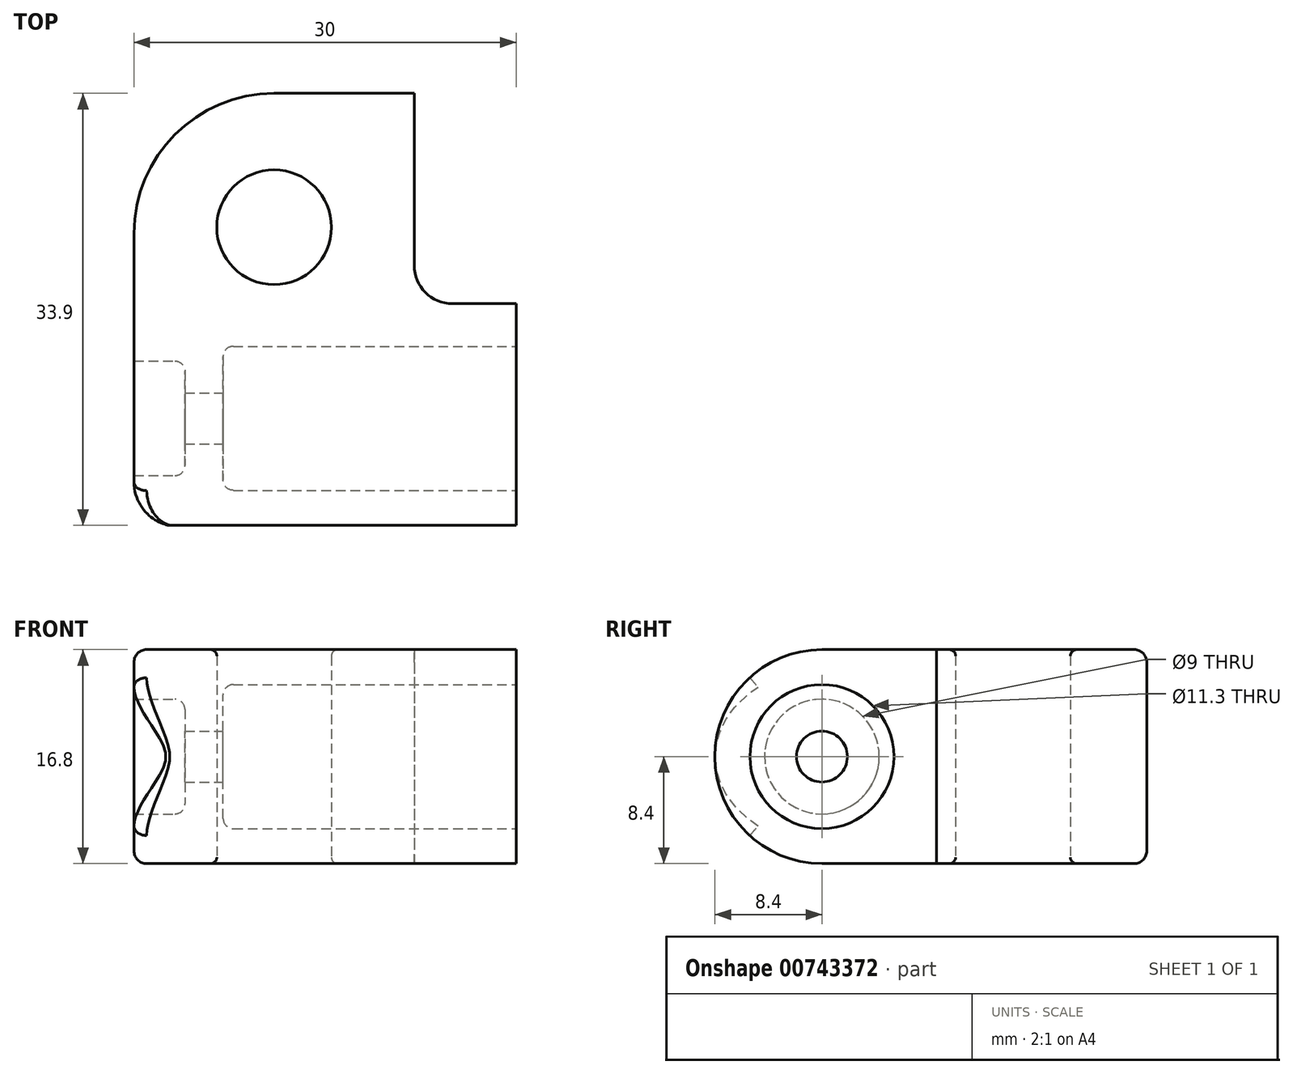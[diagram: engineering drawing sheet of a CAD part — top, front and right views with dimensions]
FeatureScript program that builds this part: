
annotation { "Feature Type Name" : "Feature", "Feature Type Description" : "" }
export const myFeature = defineFeature(function(context is Context, id is Id, definition is map)
    precondition{}
    {
        {
            var Q0;
            Q0=qCreatedBy(makeId("Top.planeOp"),FACE);
            var sketch = newSketch(context, id + "F0", { "sketchPlane" : qUnion([Q0]), "disableImprinting" : false});
            skLineSegment(sketch, "E0.bottom", {"start": v(-11, 10.5) * mm, "end": v(11, 10.5) * mm});
            skLineSegment(sketch, "E0.top", {"start": v(-11, -23.5) * mm, "end": v(19, -23.5) * mm});
            skLineSegment(sketch, "E0.left", {"start": v(-11, 10.5) * mm, "end": v(-11, -23.5) * mm});
            skLineSegment(sketch, "E0.right", {"start": v(19, -6) * mm, "end": v(19, -23.5) * mm});
            skCircle(sketch, "E1", {"center": v(0, 0) * mm, "radius": 4.5 * mm});
            skLineSegment(sketch, "E2.top", {"start": v(11, -6) * mm, "end": v(19, -6) * mm});
            skLineSegment(sketch, "E2.left", {"start": v(11, 10.5) * mm, "end": v(11, -6) * mm});
            skSolve(sketch);
        }
        {
            var Q0;
            Q0=makeQuery(id+"F0.imprint","IMPRINT",FACE,{"disambiguationData":[TD([[makeQuery(id+"F0.imprint","IMPRINT",EDGE,{"derivedFrom":sQuery(id+"F0.wireOp",EDGE,"E0.bottom")}),-1.0]])]});
            extrude(context, id + "F1", {"entities" : qUnion([Q0]), "flatOperationType" : FlatOperationType.REMOVE, "thickness1" : 5 * mm, "thickness2" : 0 * mm, "thickness" : 5 * mm, "offsetDistance" : 25 * mm, "startOffsetBound" : StartOffsetType.BLIND, "startOffsetDistance" : 25 * mm, "depth" : 16.8 * mm, "symmetric" : true, "domain" : OperationDomain.MODEL});
        }
        {
            var Q0;
            Q0=makeQuery(id+"F1.opExtrude","SWEPT_EDGE",EDGE,{"disambiguationData":[OSD([sQuery(id+"F0.wireOp",EDGE,"E2.top"),sQuery(id+"F0.wireOp",EDGE,"E2.left")])]});
            fillet(context, id + "F2", {"entities" : qUnion([Q0]), "radius" : 3 * mm, "tangentPropagation" : true, "allowEdgeOverflow" : false});
        }
        {
            var Q0;
            Q0=makeQuery(id+"F1.opExtrude","SWEPT_EDGE",EDGE,{"disambiguationData":[OSD([sQuery(id+"F0.wireOp",EDGE,"E0.bottom"),sQuery(id+"F0.wireOp",EDGE,"E0.left")])]});
            fillet(context, id + "F3", {"entities" : qUnion([Q0]), "radius" : 11 * mm, "tangentPropagation" : true, "allowEdgeOverflow" : false});
        }
        {
            var Q0;
            Q0=qCreatedBy(makeId("Top.planeOp"),FACE);
            var sketch = newSketch(context, id + "F4", { "sketchPlane" : qUnion([Q0]), "disableImprinting" : false});
            skLineSegment(sketch, "E3.0", {"start": v(-11, -0.5) * mm, "end": v(-11, -23.5) * mm});
            skPoint(sketch, "E4.trimOffspring.end.orphan", {"position": v(19, -23.5) * mm});
            skLineSegment(sketch, "E5", {"start": v(-11, -10.5) * mm, "end": v(-7, -10.5) * mm});
            skLineSegment(sketch, "E6", {"start": v(-7, -10.5) * mm, "end": v(-7, -13) * mm});
            skLineSegment(sketch, "E7", {"start": v(-7, -13) * mm, "end": v(-4, -13) * mm});
            skLineSegment(sketch, "E8", {"start": v(-4, -13) * mm, "end": v(-4, -9.35) * mm});
            skLineSegment(sketch, "E9.0", {"start": v(19, -6) * mm, "end": v(19, -23.5) * mm});
            skLineSegment(sketch, "E10", {"start": v(-4, -9.35) * mm, "end": v(19, -9.35) * mm});
            skLineSegment(sketch, "E11", {"start": v(-11, -10.5) * mm, "end": v(-11, -15) * mm});
            skLineSegment(sketch, "E12", {"start": v(19, -15) * mm, "end": v(19, -9.35) * mm});
            skLineSegment(sketch, "E13", {"start": v(-11, -15) * mm, "end": v(19, -15) * mm});
            skSolve(sketch);
        }
        {
            var Q0;
            Q0=qSketchRegion(id+"F4",true);
            var Q1;
            Q1=sQuery(id+"F4.wireOp",EDGE,"E13");
            revolve(context, id + "F5", {"operationType" : NewBodyOperationType.REMOVE, "entities" : qUnion([Q0]), "axis" : qUnion([Q1]), "revolveType" : RevolveType.FULL, "oppositeDirection" : true});
        }
        {
            var Q0;
            Q0=makeQuery(id+"F1.opExtrude","SWEPT_EDGE",EDGE,{"disambiguationData":[OSD([sQuery(id+"F0.wireOp",EDGE,"E0.top"),sQuery(id+"F0.wireOp",EDGE,"E0.left")])]});
            fillet(context, id + "F6", {"entities" : qUnion([Q0]), "radius" : 3.5 * mm, "tangentPropagation" : true, "allowEdgeOverflow" : false});
        }
        {
            var Q0;
            Q0=makeQuery(id+"F5.boolean.opBoolean","COPY",EDGE,{"derivedFrom":makeQuery(id+"F5.opRevolve","SWEPT_EDGE",EDGE,{"disambiguationData":[OSD([sQuery(id+"F4.wireOp",EDGE,"E5"),sQuery(id+"F4.wireOp",EDGE,"E11")])]})});
            var Q1;
            Q1=makeQuery(id+"F5.boolean.opBoolean","COPY",EDGE,{"derivedFrom":makeQuery(id+"F5.opRevolve","SWEPT_EDGE",EDGE,{"disambiguationData":[OSD([sQuery(id+"F4.wireOp",EDGE,"E10"),sQuery(id+"F4.wireOp",EDGE,"E12")])]})});
            fillet(context, id + "F7", {"entities" : qUnion([Q0, Q1]), "radius" : 0.8 * mm, "tangentPropagation" : true, "allowEdgeOverflow" : false});
        }
        {
            var Q0;
            Q0=makeQuery(id+"F1.opExtrude","SWEPT_FACE",FACE,{"disambiguationData":[OSD([sQuery(id+"F0.wireOp",EDGE,"E0.left")])]});
            var sketch = newSketch(context, id + "F8", { "sketchPlane" : qUnion([Q0]), "disableImprinting" : false});
            skArc(sketch, "E14", {"start": v(15, -8.4) * mm, "mid": v(23.4, 0) * mm, "end": v(15, 8.4) * mm});
            skLineSegment(sketch, "E15", {"start": v(15, 8.4) * mm, "end": v(15, 10.4) * mm});
            skLineSegment(sketch, "E16", {"start": v(15, 10.4) * mm, "end": v(24.4, 10.4) * mm});
            skLineSegment(sketch, "E17", {"start": v(24.4, 10.4) * mm, "end": v(24.4, -10.4) * mm});
            skLineSegment(sketch, "E18", {"start": v(24.4, -10.4) * mm, "end": v(15, -10.4) * mm});
            skLineSegment(sketch, "E19", {"start": v(15, -10.4) * mm, "end": v(15, -8.4) * mm});
            skSolve(sketch);
        }
        {
            var Q0;
            Q0=qSketchRegion(id+"F8",true);
            extrude(context, id + "F9", {"entities" : qUnion([Q0]), "operationType" : NewBodyOperationType.REMOVE, "endBound" : BoundingType.THROUGH_ALL, "oppositeDirection" : true, "depth" : 25 * mm});
        }
        {
            var Q0;
            Q0=makeQuery(id+"F1.opExtrude","CAP_EDGE",EDGE,{"disambiguationData":[OSD([sQuery(id+"F0.wireOp",EDGE,"E0.left")])],"isStart":true});
            var Q1;
            Q1=makeQuery(id+"F9.boolean.opBoolean","COPY",EDGE,{"disambiguationData":[OD(0.0)],"derivedFrom":makeQuery(id+"F9.opExtrude","CAP_EDGE",EDGE,{"disambiguationData":[OSD([sQuery(id+"F8.wireOp",EDGE,"E14")])],"isStart":true})});
            var Q2;
            Q2=makeQuery(id+"F9.boolean.opBoolean","INTERSECT",EDGE,{"disambiguationData":[OD(0.0)],"derivedFrom":[makeQuery(id+"F6.opFillet","BLEND_FACE",FACE,{"disambiguationData":[OSD([sQuery(id+"F0.wireOp",EDGE,"E0.top"),sQuery(id+"F0.wireOp",EDGE,"E0.left")])]}),makeQuery(id+"F9.opExtrude","SWEPT_FACE",FACE,{"disambiguationData":[OSD([sQuery(id+"F8.wireOp",EDGE,"E14")])]})]});
            var Q3;
            Q3=makeQuery(id+"F9.boolean.opBoolean","INTERSECT",EDGE,{"disambiguationData":[OD(1.0)],"derivedFrom":[makeQuery(id+"F6.opFillet","BLEND_FACE",FACE,{"disambiguationData":[OSD([sQuery(id+"F0.wireOp",EDGE,"E0.top"),sQuery(id+"F0.wireOp",EDGE,"E0.left")])]}),makeQuery(id+"F9.opExtrude","SWEPT_FACE",FACE,{"disambiguationData":[OSD([sQuery(id+"F8.wireOp",EDGE,"E14")])]})]});
            var Q4;
            Q4=makeQuery(id+"F9.boolean.opBoolean","COPY",EDGE,{"disambiguationData":[OD(1.0)],"derivedFrom":makeQuery(id+"F9.opExtrude","CAP_EDGE",EDGE,{"disambiguationData":[OSD([sQuery(id+"F8.wireOp",EDGE,"E14")])],"isStart":true})});
            var Q5;
            Q5=makeQuery(id+"F1.opExtrude","CAP_EDGE",EDGE,{"disambiguationData":[OSD([sQuery(id+"F0.wireOp",EDGE,"E0.left")])],"isStart":false});
            var Q6;
            {var subQ0=sQuery(id+"F0.wireOp",EDGE,"E0.left");var subQ1=sQuery(id+"F0.wireOp",EDGE,"E0.bottom");Q6=makeQuery(id+"F3.opFillet","BLEND_EDGE",EDGE,{"blendedFrom":[makeQuery(id+"F1.opExtrude","SWEPT_EDGE",EDGE,{"disambiguationData":[OSD([subQ1,subQ0])]}),makeQuery(id+"F1.opExtrude","CAP_FACE",FACE,{"disambiguationData":[OSD([subQ1,sQuery(id+"F0.wireOp",EDGE,"E0.top"),subQ0,sQuery(id+"F0.wireOp",EDGE,"E0.right"),sQuery(id+"F0.wireOp",EDGE,"E1"),sQuery(id+"F0.wireOp",EDGE,"E2.top"),sQuery(id+"F0.wireOp",EDGE,"E2.left")])],"isStart":true})],"blendedInto":[makeQuery(id+"F1.opExtrude","CAP_FACE",FACE,{"disambiguationData":[OSD([subQ1,sQuery(id+"F0.wireOp",EDGE,"E0.top"),subQ0,sQuery(id+"F0.wireOp",EDGE,"E0.right"),sQuery(id+"F0.wireOp",EDGE,"E1"),sQuery(id+"F0.wireOp",EDGE,"E2.top"),sQuery(id+"F0.wireOp",EDGE,"E2.left")])],"isStart":true})]});}
            var Q7;
            {var subQ0=sQuery(id+"F0.wireOp",EDGE,"E0.left");var subQ1=sQuery(id+"F0.wireOp",EDGE,"E0.bottom");Q7=makeQuery(id+"F3.opFillet","BLEND_EDGE",EDGE,{"blendedFrom":[makeQuery(id+"F1.opExtrude","SWEPT_EDGE",EDGE,{"disambiguationData":[OSD([subQ1,subQ0])]}),makeQuery(id+"F1.opExtrude","CAP_FACE",FACE,{"disambiguationData":[OSD([subQ1,sQuery(id+"F0.wireOp",EDGE,"E0.top"),subQ0,sQuery(id+"F0.wireOp",EDGE,"E0.right"),sQuery(id+"F0.wireOp",EDGE,"E1"),sQuery(id+"F0.wireOp",EDGE,"E2.top"),sQuery(id+"F0.wireOp",EDGE,"E2.left")])],"isStart":false})],"blendedInto":[makeQuery(id+"F1.opExtrude","CAP_FACE",FACE,{"disambiguationData":[OSD([subQ1,sQuery(id+"F0.wireOp",EDGE,"E0.top"),subQ0,sQuery(id+"F0.wireOp",EDGE,"E0.right"),sQuery(id+"F0.wireOp",EDGE,"E1"),sQuery(id+"F0.wireOp",EDGE,"E2.top"),sQuery(id+"F0.wireOp",EDGE,"E2.left")])],"isStart":false})]});}
            var Q8;
            Q8=makeQuery(id+"F1.opExtrude","CAP_EDGE",EDGE,{"disambiguationData":[OSD([sQuery(id+"F0.wireOp",EDGE,"E0.bottom")])],"isStart":true});
            var Q9;
            Q9=makeQuery(id+"F1.opExtrude","CAP_EDGE",EDGE,{"disambiguationData":[OSD([sQuery(id+"F0.wireOp",EDGE,"E0.bottom")])],"isStart":false});
            fillet(context, id + "F10", {"entities" : qUnion([Q0, Q1, Q2, Q3, Q4, Q5, Q6, Q7, Q8, Q9]), "radius" : 1 * mm, "tangentPropagation" : true, "allowEdgeOverflow" : false});
        }
        {
            var Q0;
            Q0=makeQuery(id+"F1.opExtrude","CAP_EDGE",EDGE,{"disambiguationData":[OSD([sQuery(id+"F0.wireOp",EDGE,"E1")])],"isStart":true});
            var Q1;
            Q1=makeQuery(id+"F1.opExtrude","CAP_EDGE",EDGE,{"disambiguationData":[OSD([sQuery(id+"F0.wireOp",EDGE,"E1")])],"isStart":false});
            fillet(context, id + "F11", {"entities" : qUnion([Q0, Q1]), "radius" : 0.5 * mm, "tangentPropagation" : true, "allowEdgeOverflow" : false});
        }
    });
